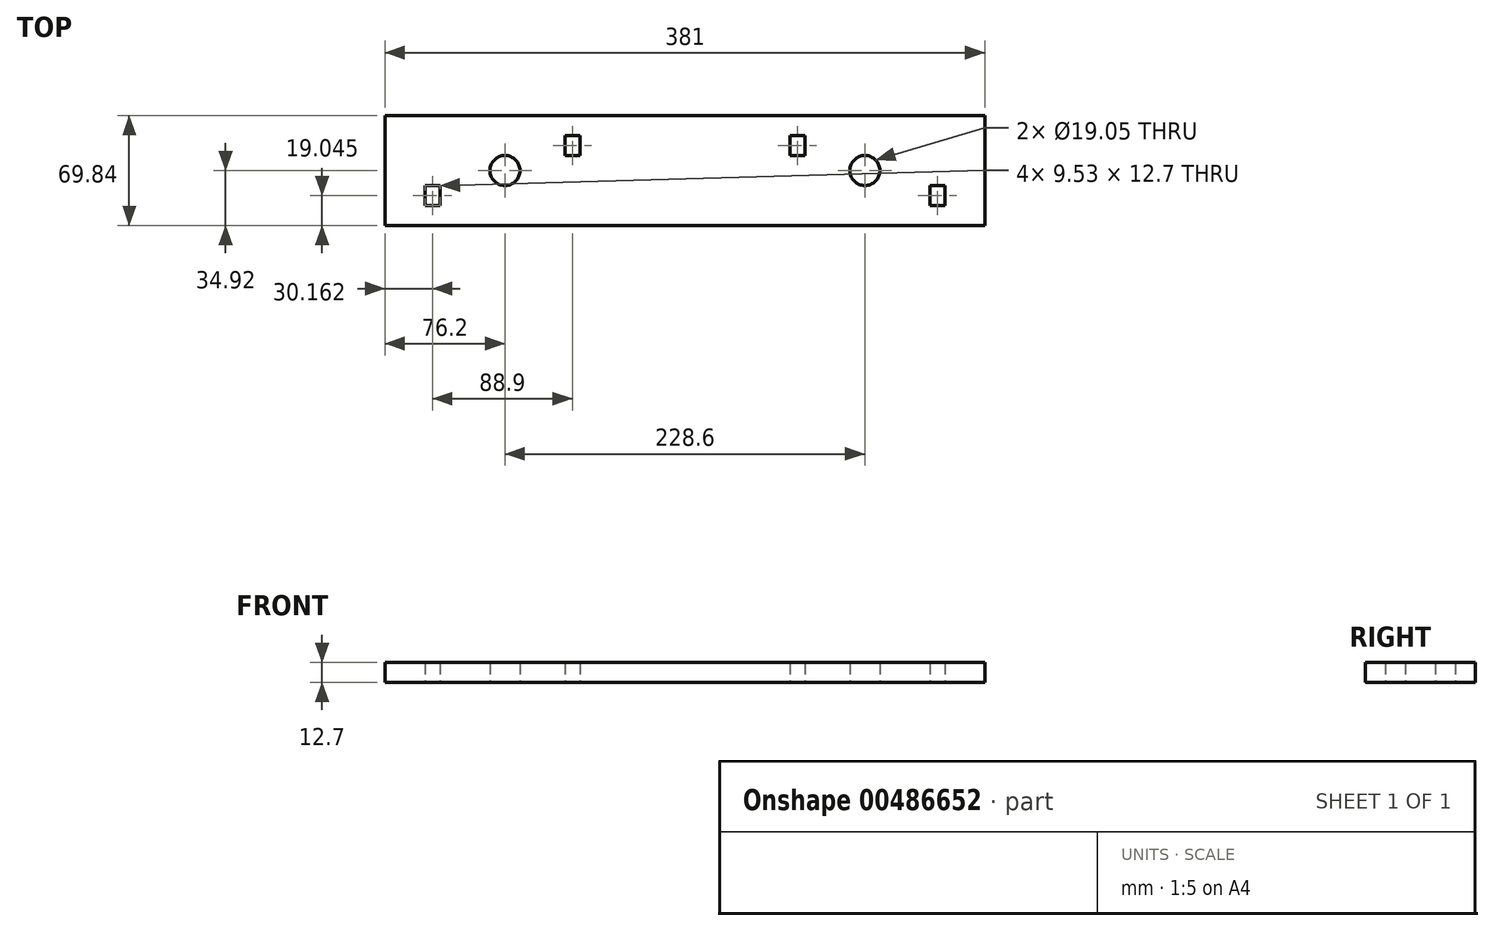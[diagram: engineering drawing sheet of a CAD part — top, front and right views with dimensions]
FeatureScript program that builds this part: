
annotation { "Feature Type Name" : "Feature", "Feature Type Description" : "" }
export const myFeature = defineFeature(function(context is Context, id is Id, definition is map)
    precondition{}
    {
        {
            var Q0;
            Q0=qCreatedBy(makeId("Top.planeOp"),FACE);
            var sketch = newSketch(context, id + "F0", { "sketchPlane" : qUnion([Q0])});
            skLineSegment(sketch, "E0.bottom", {"start": v(-190.5, 34.93) * mm, "end": v(190.5, 34.93) * mm});
            skLineSegment(sketch, "E0.top", {"start": v(-190.5, -34.93) * mm, "end": v(190.5, -34.93) * mm});
            skLineSegment(sketch, "E0.left", {"start": v(-190.5, 34.93) * mm, "end": v(-190.5, -34.93) * mm});
            skLineSegment(sketch, "E0.right", {"start": v(190.5, 34.93) * mm, "end": v(190.5, -34.93) * mm});
            skPoint(sketch, "E0.middle", {"position": v(0, 0) * mm});
            skLineSegment(sketch, "E1.bottom", {"start": v(-165.1, -9.53) * mm, "end": v(-155.58, -9.53) * mm});
            skLineSegment(sketch, "E1.top", {"start": v(-165.1, -22.23) * mm, "end": v(-155.58, -22.23) * mm});
            skLineSegment(sketch, "E1.left", {"start": v(-165.1, -9.53) * mm, "end": v(-165.1, -22.23) * mm});
            skLineSegment(sketch, "E1.right", {"start": v(-155.58, -9.53) * mm, "end": v(-155.58, -22.23) * mm});
            skPoint(sketch, "E1.middle", {"position": v(-160.34, -15.88) * mm});
            skPoint(sketch, "E2.MirrorP", {"position": v(160.34, -15.88) * mm});
            skLineSegment(sketch, "E3.MirrorCS", {"start": v(165.1, -9.53) * mm, "end": v(155.58, -9.53) * mm});
            skLineSegment(sketch, "E4.MirrorCS", {"start": v(165.1, -9.53) * mm, "end": v(165.1, -22.23) * mm});
            skLineSegment(sketch, "E5.MirrorCS", {"start": v(155.58, -9.53) * mm, "end": v(155.58, -22.23) * mm});
            skLineSegment(sketch, "E6.MirrorCS", {"start": v(165.1, -22.23) * mm, "end": v(155.58, -22.23) * mm});
            skCircle(sketch, "E7", {"center": v(-114.3, 0) * mm, "radius": 9.53 * mm});
            skCircle(sketch, "E8.MirrorC", {"center": v(114.3, 0) * mm, "radius": 9.53 * mm});
            skLineSegment(sketch, "E9.bottom", {"start": v(-76.2, 22.22) * mm, "end": v(-66.68, 22.22) * mm});
            skLineSegment(sketch, "E9.top", {"start": v(-76.2, 9.52) * mm, "end": v(-66.68, 9.52) * mm});
            skLineSegment(sketch, "E9.left", {"start": v(-76.2, 22.22) * mm, "end": v(-76.2, 9.52) * mm});
            skLineSegment(sketch, "E9.right", {"start": v(-66.68, 22.22) * mm, "end": v(-66.68, 9.52) * mm});
            skPoint(sketch, "E9.middle", {"position": v(-71.44, 15.87) * mm});
            skLineSegment(sketch, "E10.MirrorCS", {"start": v(66.68, 22.22) * mm, "end": v(66.68, 9.52) * mm});
            skLineSegment(sketch, "E11.MirrorCS", {"start": v(76.2, 9.52) * mm, "end": v(66.68, 9.52) * mm});
            skPoint(sketch, "E12.MirrorP", {"position": v(71.44, 15.87) * mm});
            skLineSegment(sketch, "E13.MirrorCS", {"start": v(76.2, 22.22) * mm, "end": v(66.68, 22.22) * mm});
            skLineSegment(sketch, "E14.MirrorCS", {"start": v(76.2, 22.22) * mm, "end": v(76.2, 9.52) * mm});
            skPoint(sketch, "E15", {"position": v(19.05, 0) * mm});
            skPoint(sketch, "E16.MirrorP", {"position": v(-19.05, 0) * mm});
            skLineSegment(sketch, "E17", {"start": v(-19.05, 0) * mm, "end": v(19.05, 0) * mm});
            skSolve(sketch);
        }
        {
            var Q0;
            Q0=makeQuery(id+"F0.imprint","IMPRINT",FACE,{"disambiguationData":[TD([[makeQuery(id+"F0.imprint","IMPRINT",EDGE,{"derivedFrom":sQuery(id+"F0.wireOp",EDGE,"E0.bottom")}),-1.0]])]});
            extrude(context, id + "F1", {"entities" : qUnion([Q0]), "depth" : 12.7 * mm});
        }
    });
